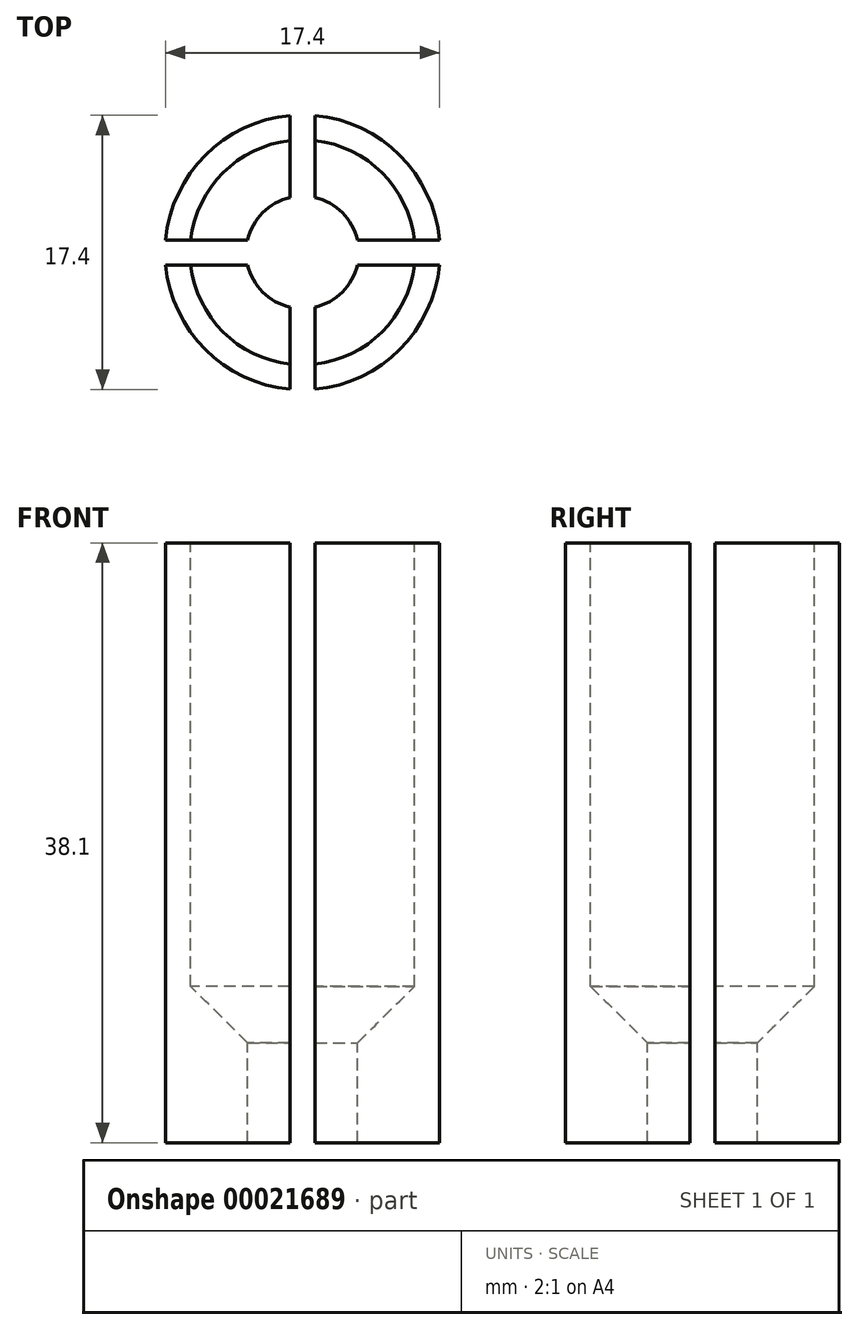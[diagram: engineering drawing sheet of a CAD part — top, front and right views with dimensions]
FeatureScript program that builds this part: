
annotation { "Feature Type Name" : "Feature", "Feature Type Description" : "" }
export const myFeature = defineFeature(function(context is Context, id is Id, definition is map)
    precondition{}
    {
        {
            var Q0;
            Q0=qCreatedBy(makeId("Front.planeOp"),FACE);
            var sketch = newSketch(context, id + "F0", { "sketchPlane" : qUnion([Q0])});
            skLineSegment(sketch, "E0", {"start": v(-8.48, 0) * mm, "end": v(9.24, 0) * mm, "construction": true});
            skLineSegment(sketch, "E1", {"start": v(-7.14, 9.92) * mm, "end": v(-3.57, 6.35) * mm});
            skLineSegment(sketch, "E2", {"start": v(-3.57, 6.35) * mm, "end": v(-3.57, 0) * mm});
            skLineSegment(sketch, "E3", {"start": v(0, 15.22) * mm, "end": v(0, -6.5) * mm, "construction": true});
            skLineSegment(sketch, "E4", {"start": v(-3.57, 0) * mm, "end": v(-8.73, 0) * mm});
            skLineSegment(sketch, "E5", {"start": v(-7.14, 9.92) * mm, "end": v(-7.14, 38.1) * mm});
            skLineSegment(sketch, "E6", {"start": v(-7.14, 38.1) * mm, "end": v(-8.73, 38.1) * mm});
            skLineSegment(sketch, "E7", {"start": v(-8.73, 0) * mm, "end": v(-8.73, 38.1) * mm});
            skSolve(sketch);
        }
        {
            var Q0;
            Q0=makeQuery(id+"F0.imprint","IMPRINT",FACE,{"disambiguationData":[TD([[makeQuery(id+"F0.imprint","IMPRINT",EDGE,{"derivedFrom":sQuery(id+"F0.wireOp",EDGE,"54762abc-a060-42b1-878a-edc13b85bfc6")}),-1.0]])]});
            var Q1;
            Q1=makeQuery(id+"F0.imprint","IMPRINT",FACE,{"disambiguationData":[TD([[makeQuery(id+"F0.imprint","IMPRINT",EDGE,{"derivedFrom":sQuery(id+"F0.wireOp",EDGE,"E1")}),-1.0]])]});
            var Q2;
            Q2=sQuery(id+"F0.wireOp",EDGE,"E3");
            revolve(context, id + "F1", {"entities" : qUnion([Q0, Q1]), "axis" : qUnion([Q2]), "revolveType" : RevolveType.FULL});
        }
        {
            var Q0;
            Q0=qCreatedBy(makeId("Top.planeOp"),FACE);
            var sketch = newSketch(context, id + "F2", { "sketchPlane" : qUnion([Q0])});
            skLineSegment(sketch, "E8", {"start": v(15.74, 0) * mm, "end": v(-17.53, 0) * mm, "construction": true});
            skLineSegment(sketch, "E9", {"start": v(0, -14.8) * mm, "end": v(0, 14.79) * mm, "construction": true});
            skLineSegment(sketch, "E10", {"start": v(-0.8, 8.73) * mm, "end": v(-0.8, 0.8) * mm});
            skLineSegment(sketch, "E11", {"start": v(-0.8, 0.8) * mm, "end": v(-8.73, 0.8) * mm});
            skLineSegment(sketch, "E12", {"start": v(-8.73, 0.8) * mm, "end": v(-8.73, -0.8) * mm});
            skLineSegment(sketch, "E13", {"start": v(-8.73, -0.8) * mm, "end": v(-0.8, -0.8) * mm});
            skLineSegment(sketch, "E14", {"start": v(-0.8, -0.8) * mm, "end": v(-0.8, -8.73) * mm});
            skLineSegment(sketch, "E15", {"start": v(-0.8, -8.73) * mm, "end": v(0.8, -8.73) * mm});
            skLineSegment(sketch, "E16", {"start": v(0.8, -8.73) * mm, "end": v(0.8, -0.8) * mm});
            skLineSegment(sketch, "E17", {"start": v(0.8, -0.8) * mm, "end": v(8.73, -0.8) * mm});
            skLineSegment(sketch, "E18", {"start": v(8.73, -0.8) * mm, "end": v(8.73, 0.8) * mm});
            skLineSegment(sketch, "E19", {"start": v(8.73, 0.8) * mm, "end": v(0.8, 0.8) * mm});
            skLineSegment(sketch, "E20", {"start": v(0.8, 0.8) * mm, "end": v(0.8, 8.73) * mm});
            skLineSegment(sketch, "E21", {"start": v(0.8, 8.73) * mm, "end": v(-0.8, 8.73) * mm});
            skSolve(sketch);
        }
        {
            var Q0;
            Q0 = qSketchRegion(id + "F2", true);
            extrude(context, id + "F3", {"entities" : qUnion([Q0]), "operationType" : NewBodyOperationType.REMOVE, "endBound" : BoundingType.THROUGH_ALL, "depth" : 25.4 * mm});
        }
    });
